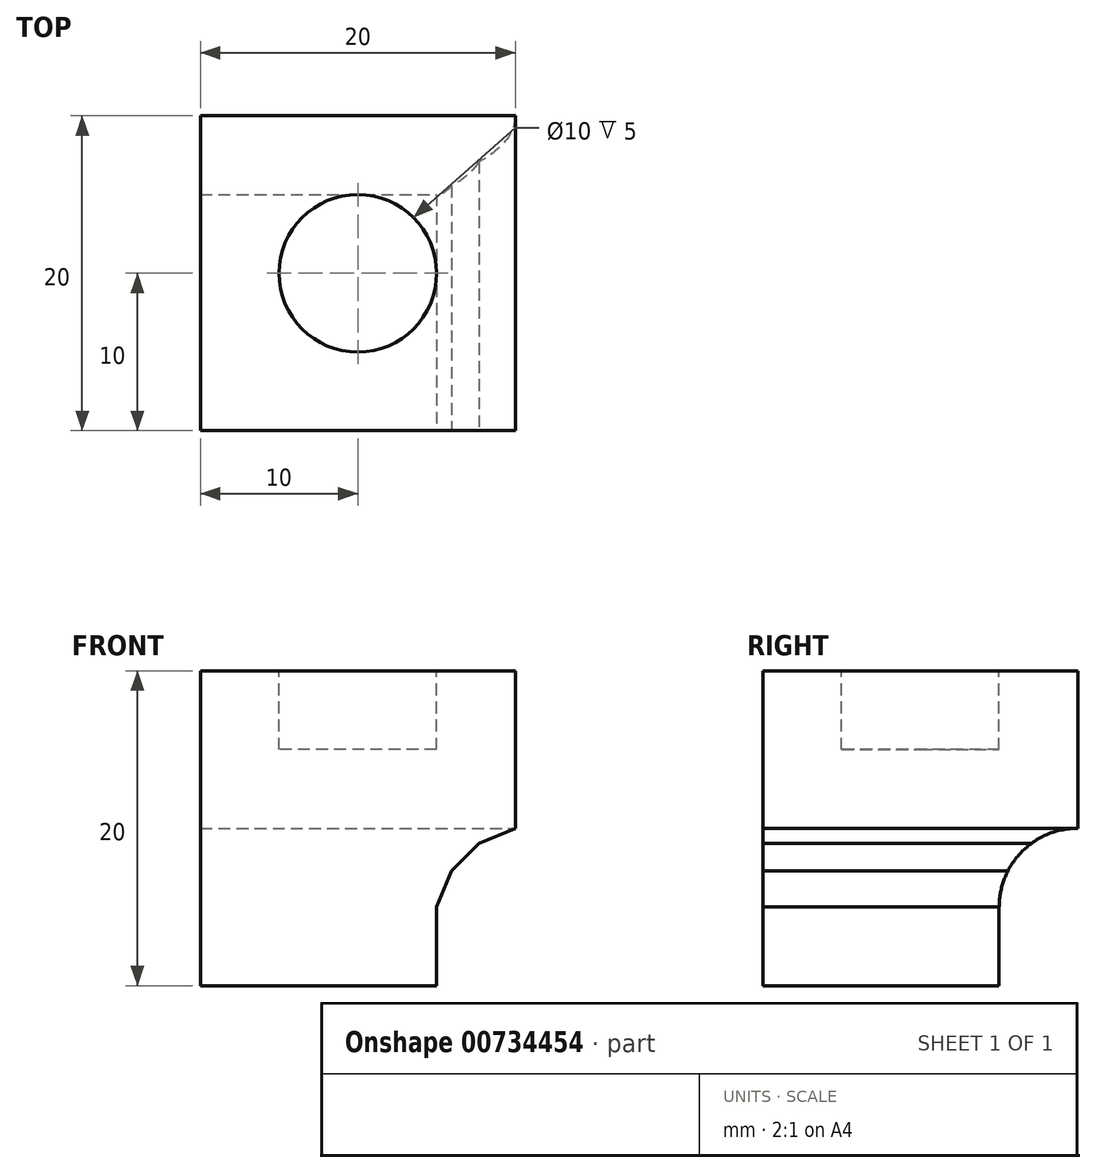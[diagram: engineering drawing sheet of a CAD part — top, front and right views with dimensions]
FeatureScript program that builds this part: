
annotation { "Feature Type Name" : "Feature", "Feature Type Description" : "" }
export const myFeature = defineFeature(function(context is Context, id is Id, definition is map)
    precondition{}
    {
        {
            var Q0;
            Q0=qCreatedBy(makeId("Top.planeOp"),FACE);
            var sketch = newSketch(context, id + "F0", { "sketchPlane" : qUnion([Q0])});
            skLineSegment(sketch, "E0.bottom", {"start": v(-10, 10) * mm, "end": v(10, 10) * mm});
            skLineSegment(sketch, "E0.top", {"start": v(-10, -10) * mm, "end": v(10, -10) * mm});
            skLineSegment(sketch, "E0.left", {"start": v(-10, 10) * mm, "end": v(-10, -10) * mm});
            skLineSegment(sketch, "E0.right", {"start": v(10, 10) * mm, "end": v(10, -10) * mm});
            skLineSegment(sketch, "E1", {"start": v(-10, 10) * mm, "end": v(10, -10) * mm, "construction": true});
            skSolve(sketch);
        }
        {
            var Q0;
            Q0 = qSketchRegion(id + "F0", true);
            extrude(context, id + "F1", {"entities" : qUnion([Q0]), "depth" : 20 * mm, "offsetDistance" : 25 * mm});
        }
        {
            var Q0;
            Q0=qCreatedBy(makeId("Front.planeOp"),FACE);
            var sketch = newSketch(context, id + "F2", { "sketchPlane" : qUnion([Q0])});
            skLineSegment(sketch, "E2", {"start": v(5, 0) * mm, "end": v(5, 5) * mm});
            skLineSegment(sketch, "E3", {"start": v(5, 5) * mm, "end": v(5.95, 7.3) * mm});
            skLineSegment(sketch, "E4", {"start": v(5.95, 7.3) * mm, "end": v(7.7, 9.05) * mm});
            skLineSegment(sketch, "E5", {"start": v(7.7, 9.05) * mm, "end": v(10, 10) * mm});
            skLineSegment(sketch, "E6", {"start": v(10, 10) * mm, "end": v(10, 0) * mm});
            skLineSegment(sketch, "E7", {"start": v(10, 0) * mm, "end": v(5, 0) * mm});
            skSolve(sketch);
        }
        {
            var Q0;
            Q0 = qSketchRegion(id + "F2", true);
            extrude(context, id + "F3", {"entities" : qUnion([Q0]), "operationType" : NewBodyOperationType.REMOVE, "endBound" : BoundingType.THROUGH_ALL, "oppositeDirection" : true, "depth" : 25 * mm, "offsetDistance" : 25 * mm, "hasSecondDirection" : true, "secondDirectionBound" : SecondDirectionBoundingType.THROUGH_ALL, "secondDirectionOppositeDirection" : false, "secondDirectionDepth" : 25 * mm});
        }
        {
            var Q0;
            Q0=qCreatedBy(makeId("Right.planeOp"),FACE);
            var sketch = newSketch(context, id + "F4", { "sketchPlane" : qUnion([Q0])});
            skLineSegment(sketch, "E8", {"start": v(5, 0) * mm, "end": v(5, 5) * mm});
            skLineSegment(sketch, "E9", {"start": v(10, 10) * mm, "end": v(10, 0) * mm});
            skLineSegment(sketch, "E10", {"start": v(10, 0) * mm, "end": v(5, 0) * mm});
            skArc(sketch, "E11", {"start": v(10, 10) * mm, "mid": v(6.46, 8.54) * mm, "end": v(5, 5) * mm});
            skSolve(sketch);
        }
        {
            var Q0;
            Q0 = qSketchRegion(id + "F4", true);
            extrude(context, id + "F5", {"entities" : qUnion([Q0]), "operationType" : NewBodyOperationType.REMOVE, "endBound" : BoundingType.THROUGH_ALL, "oppositeDirection" : true, "depth" : 25 * mm, "offsetDistance" : 25 * mm, "hasSecondDirection" : true, "secondDirectionBound" : SecondDirectionBoundingType.THROUGH_ALL, "secondDirectionOppositeDirection" : false, "secondDirectionDepth" : 25 * mm});
        }
        {
            var Q0;
            Q0=makeQuery(id+"F1.opExtrude","CAP_FACE",FACE,{"disambiguationData":[OSD([sQuery(id+"F0.wireOp",EDGE,"E0.bottom"),sQuery(id+"F0.wireOp",EDGE,"E0.top"),sQuery(id+"F0.wireOp",EDGE,"E0.left"),sQuery(id+"F0.wireOp",EDGE,"E0.right")])],"isStart":false});
            var sketch = newSketch(context, id + "F6", { "sketchPlane" : qUnion([Q0])});
            skCircle(sketch, "E12", {"center": v(0, 0) * mm, "radius": 5 * mm});
            skSolve(sketch);
        }
        {
            var Q0;
            Q0 = qSketchRegion(id + "F6", true);
            extrude(context, id + "F7", {"entities" : qUnion([Q0]), "operationType" : NewBodyOperationType.REMOVE, "oppositeDirection" : true, "depth" : 5 * mm, "offsetDistance" : 25 * mm});
        }
    });
